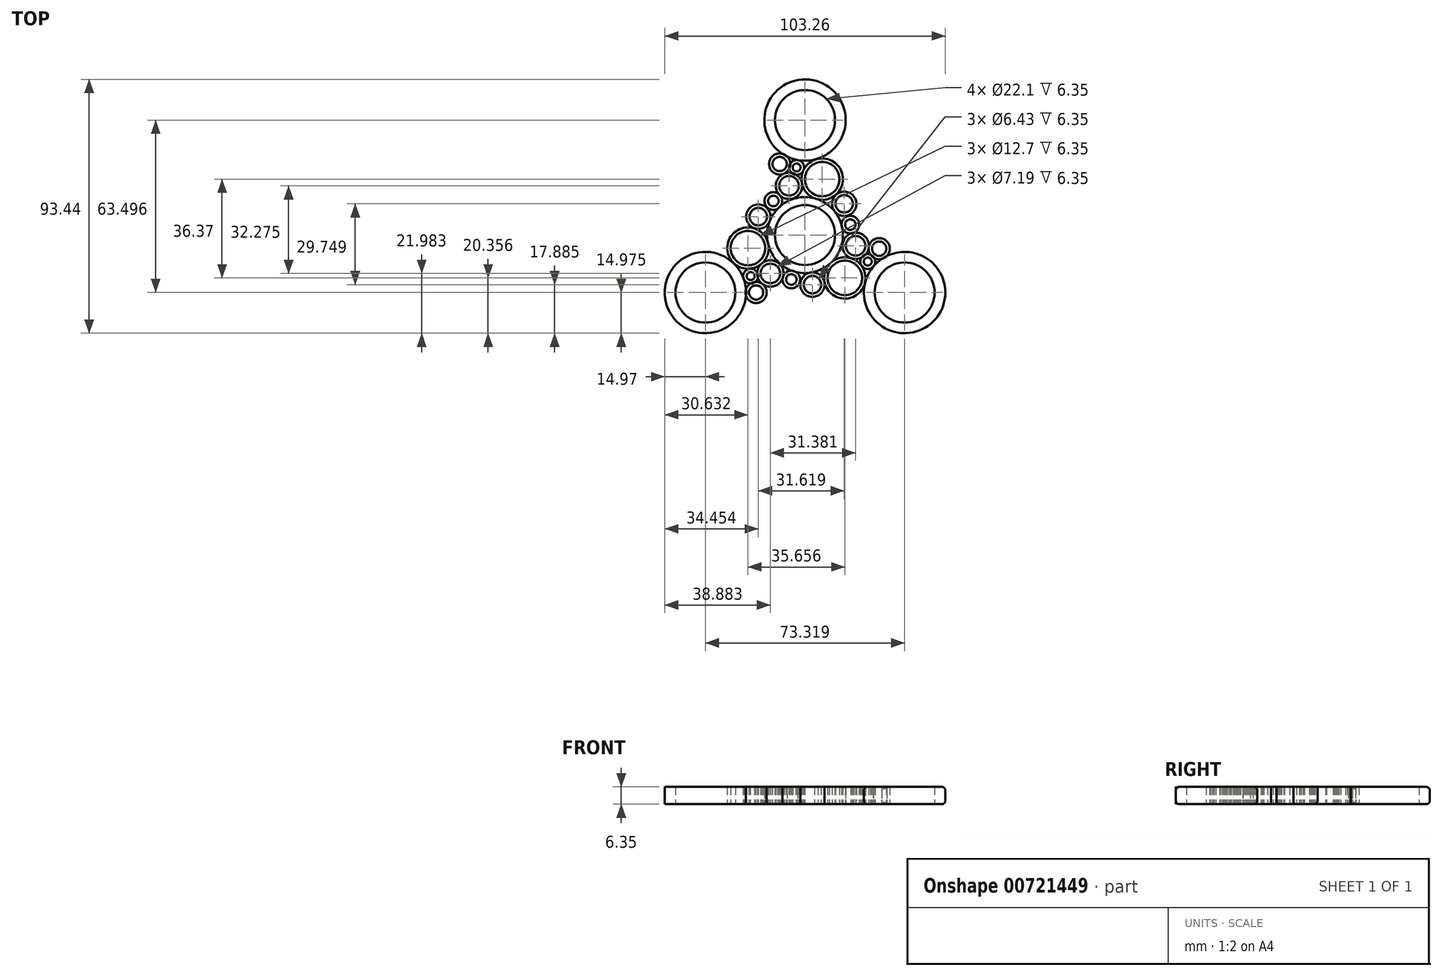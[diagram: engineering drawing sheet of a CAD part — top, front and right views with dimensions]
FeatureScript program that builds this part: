
annotation { "Feature Type Name" : "Feature", "Feature Type Description" : "" }
export const myFeature = defineFeature(function(context is Context, id is Id, definition is map)
    precondition{}
    {
        {
            var Q0;
            Q0=qCreatedBy(makeId("Top.planeOp"),FACE);
            var sketch = newSketch(context, id + "F0", { "sketchPlane" : qUnion([Q0])});
            skCircle(sketch, "E0", {"center": v(0, 0) * mm, "radius": 11.05 * mm});
            skCircle(sketch, "E1", {"center": v(0, 0) * mm, "radius": 13.97 * mm});
            skPoint(sketch, "E2", {"position": v(3.65, 13.49) * mm});
            skCircle(sketch, "E3", {"center": v(6.34, 20.59) * mm, "radius": 7.62 * mm});
            skCircle(sketch, "E4", {"center": v(6.34, 20.59) * mm, "radius": 6.35 * mm});
            skPoint(sketch, "E5", {"position": v(-4.32, 13.29) * mm});
            skPoint(sketch, "E6", {"position": v(-1.17, 19.27) * mm});
            skCircle(sketch, "E7", {"center": v(-5.89, 18.12) * mm, "radius": 4.86 * mm});
            skPoint(sketch, "E8", {"position": v(3.38, 27.75) * mm});
            skCircle(sketch, "E9", {"center": v(0, 42.33) * mm, "radius": 14.97 * mm});
            skCircle(sketch, "E10", {"center": v(0, 42.33) * mm, "radius": 11.05 * mm});
            skPoint(sketch, "E11", {"position": v(-7.51, 22.7) * mm});
            skPoint(sketch, "E12", {"position": v(-6, 24.88) * mm});
            skPoint(sketch, "E13", {"position": v(-7.86, 29.6) * mm});
            skPoint(sketch, "E14", {"position": v(-10.07, 9.68) * mm});
            skCircle(sketch, "E15", {"center": v(-11.66, 12.53) * mm, "radius": 3.26 * mm});
            skCircle(sketch, "E16", {"center": v(-5.89, 18.12) * mm, "radius": 3.6 * mm});
            skPoint(sketch, "E17", {"position": v(-8.94, 14.34) * mm});
            skCircle(sketch, "E18", {"center": v(-11.66, 12.53) * mm, "radius": 1.94 * mm});
            skPoint(sketch, "E19", {"position": v(-3.65, 22.43) * mm});
            skPoint(sketch, "E20", {"position": v(-0.52, 23.91) * mm});
            skCircle(sketch, "E21", {"center": v(-9.31, 26.15) * mm, "radius": 3.9 * mm});
            skCircle(sketch, "E22", {"center": v(-3.09, 24.88) * mm, "radius": 2.75 * mm});
            skPoint(sketch, "E23", {"position": v(-2.54, 27.58) * mm});
            skCircle(sketch, "E24", {"center": v(-3.09, 24.88) * mm, "radius": 1.47 * mm});
            skCircle(sketch, "E25", {"center": v(-9.31, 26.15) * mm, "radius": 2.63 * mm});
            skCircle(sketch, "E26.1.0", {"center": v(-36.66, -21.17) * mm, "radius": 11.05 * mm});
            skCircle(sketch, "E26.2.0", {"center": v(36.66, -21.17) * mm, "radius": 11.05 * mm});
            skCircle(sketch, "E27.1.0", {"center": v(-36.66, -21.17) * mm, "radius": 14.97 * mm});
            skCircle(sketch, "E27.2.0", {"center": v(36.66, -21.17) * mm, "radius": 14.97 * mm});
            skCircle(sketch, "E28.1.0", {"center": v(-21, -4.8) * mm, "radius": 7.62 * mm});
            skCircle(sketch, "E28.2.0", {"center": v(14.66, -15.78) * mm, "radius": 7.62 * mm});
            skCircle(sketch, "E29.1.0", {"center": v(-21, -4.8) * mm, "radius": 6.35 * mm});
            skCircle(sketch, "E29.2.0", {"center": v(14.66, -15.78) * mm, "radius": 6.35 * mm});
            skCircle(sketch, "E30.1.0", {"center": v(-12.75, -14.16) * mm, "radius": 4.86 * mm});
            skCircle(sketch, "E30.2.0", {"center": v(18.63, -3.96) * mm, "radius": 4.86 * mm});
            skCircle(sketch, "E31.1.0", {"center": v(-12.75, -14.16) * mm, "radius": 3.6 * mm});
            skCircle(sketch, "E31.2.0", {"center": v(18.63, -3.96) * mm, "radius": 3.6 * mm});
            skCircle(sketch, "E32.1.0", {"center": v(-5.02, -16.36) * mm, "radius": 3.26 * mm});
            skCircle(sketch, "E32.2.0", {"center": v(16.68, 3.83) * mm, "radius": 3.26 * mm});
            skCircle(sketch, "E33.1.0", {"center": v(-5.02, -16.36) * mm, "radius": 1.94 * mm});
            skCircle(sketch, "E33.2.0", {"center": v(16.68, 3.83) * mm, "radius": 1.94 * mm});
            skCircle(sketch, "E34.1.0", {"center": v(-20, -15.11) * mm, "radius": 2.75 * mm});
            skCircle(sketch, "E34.2.0", {"center": v(23.1, -9.77) * mm, "radius": 2.75 * mm});
            skCircle(sketch, "E35.1.0", {"center": v(-20, -15.11) * mm, "radius": 1.47 * mm});
            skCircle(sketch, "E35.2.0", {"center": v(23.1, -9.77) * mm, "radius": 1.47 * mm});
            skCircle(sketch, "E36.1.0", {"center": v(-18, -21.14) * mm, "radius": 3.9 * mm});
            skCircle(sketch, "E36.2.0", {"center": v(27.3, -5.01) * mm, "radius": 3.9 * mm});
            skCircle(sketch, "E37.1.0", {"center": v(-18, -21.14) * mm, "radius": 2.63 * mm});
            skCircle(sketch, "E37.2.0", {"center": v(27.3, -5.01) * mm, "radius": 2.63 * mm});
            skCircle(sketch, "E38", {"center": v(14.44, 11.5) * mm, "radius": 4.49 * mm});
            skPoint(sketch, "E39", {"position": v(15.34, 6.8) * mm});
            skCircle(sketch, "E40", {"center": v(14.44, 11.5) * mm, "radius": 3.21 * mm});
            skCircle(sketch, "E41.1.0", {"center": v(-17.18, 6.76) * mm, "radius": 4.49 * mm});
            skCircle(sketch, "E41.2.0", {"center": v(2.73, -18.26) * mm, "radius": 4.49 * mm});
            skCircle(sketch, "E42.1.0", {"center": v(-17.18, 6.76) * mm, "radius": 3.21 * mm});
            skCircle(sketch, "E42.2.0", {"center": v(2.73, -18.26) * mm, "radius": 3.21 * mm});
            skSolve(sketch);
        }
        {
            var Q0;
            Q0=makeQuery(id+"F0.imprint","IMPRINT",FACE,{"disambiguationData":[TD([[makeQuery(id+"F0.imprint","IMPRINT",EDGE,{"derivedFrom":sQuery(id+"F0.wireOp",EDGE,"E26.1.0")}),-1.0]])]});
            var Q1;
            Q1=makeQuery(id+"F0.imprint","IMPRINT",FACE,{"disambiguationData":[TD([[makeQuery(id+"F0.imprint","IMPRINT",EDGE,{"derivedFrom":sQuery(id+"F0.wireOp",EDGE,"E37.1.0")}),-1.0]])]});
            var Q2;
            Q2=makeQuery(id+"F0.imprint","IMPRINT",FACE,{"disambiguationData":[TD([[makeQuery(id+"F0.imprint","IMPRINT",EDGE,{"derivedFrom":sQuery(id+"F0.wireOp",EDGE,"E35.1.0")}),-1.0]])]});
            var Q3;
            Q3=makeQuery(id+"F0.imprint","IMPRINT",FACE,{"disambiguationData":[TD([[makeQuery(id+"F0.imprint","IMPRINT",EDGE,{"derivedFrom":sQuery(id+"F0.wireOp",EDGE,"E29.1.0")}),-1.0]])]});
            var Q4;
            Q4=makeQuery(id+"F0.imprint","IMPRINT",FACE,{"disambiguationData":[TD([[makeQuery(id+"F0.imprint","IMPRINT",EDGE,{"derivedFrom":sQuery(id+"F0.wireOp",EDGE,"E31.1.0")}),-1.0]])]});
            var Q5;
            Q5=makeQuery(id+"F0.imprint","IMPRINT",FACE,{"disambiguationData":[TD([[makeQuery(id+"F0.imprint","IMPRINT",EDGE,{"derivedFrom":sQuery(id+"F0.wireOp",EDGE,"E33.1.0")}),-1.0]])]});
            var Q6;
            Q6=makeQuery(id+"F0.imprint","IMPRINT",FACE,{"disambiguationData":[TD([[makeQuery(id+"F0.imprint","IMPRINT",EDGE,{"derivedFrom":sQuery(id+"F0.wireOp",EDGE,"E0")}),-1.0]])]});
            var Q7;
            Q7=makeQuery(id+"F0.imprint","IMPRINT",FACE,{"disambiguationData":[TD([[makeQuery(id+"F0.imprint","IMPRINT",EDGE,{"derivedFrom":sQuery(id+"F0.wireOp",EDGE,"E29.2.0")}),-1.0]])]});
            var Q8;
            Q8=makeQuery(id+"F0.imprint","IMPRINT",FACE,{"disambiguationData":[TD([[makeQuery(id+"F0.imprint","IMPRINT",EDGE,{"derivedFrom":sQuery(id+"F0.wireOp",EDGE,"E26.2.0")}),-1.0]])]});
            var Q9;
            Q9=makeQuery(id+"F0.imprint","IMPRINT",FACE,{"disambiguationData":[TD([[makeQuery(id+"F0.imprint","IMPRINT",EDGE,{"derivedFrom":sQuery(id+"F0.wireOp",EDGE,"E35.2.0")}),-1.0]])]});
            var Q10;
            Q10=makeQuery(id+"F0.imprint","IMPRINT",FACE,{"disambiguationData":[TD([[makeQuery(id+"F0.imprint","IMPRINT",EDGE,{"derivedFrom":sQuery(id+"F0.wireOp",EDGE,"E37.2.0")}),-1.0]])]});
            var Q11;
            Q11=makeQuery(id+"F0.imprint","IMPRINT",FACE,{"disambiguationData":[TD([[makeQuery(id+"F0.imprint","IMPRINT",EDGE,{"derivedFrom":sQuery(id+"F0.wireOp",EDGE,"E31.2.0")}),-1.0]])]});
            var Q12;
            Q12=makeQuery(id+"F0.imprint","IMPRINT",FACE,{"disambiguationData":[TD([[makeQuery(id+"F0.imprint","IMPRINT",EDGE,{"derivedFrom":sQuery(id+"F0.wireOp",EDGE,"E33.2.0")}),-1.0]])]});
            var Q13;
            Q13=makeQuery(id+"F0.imprint","IMPRINT",FACE,{"disambiguationData":[TD([[makeQuery(id+"F0.imprint","IMPRINT",EDGE,{"derivedFrom":sQuery(id+"F0.wireOp",EDGE,"E4")}),-1.0]])]});
            var Q14;
            Q14=makeQuery(id+"F0.imprint","IMPRINT",FACE,{"disambiguationData":[TD([[makeQuery(id+"F0.imprint","IMPRINT",EDGE,{"derivedFrom":sQuery(id+"F0.wireOp",EDGE,"E16")}),-1.0]])]});
            var Q15;
            Q15=makeQuery(id+"F0.imprint","IMPRINT",FACE,{"disambiguationData":[TD([[makeQuery(id+"F0.imprint","IMPRINT",EDGE,{"derivedFrom":sQuery(id+"F0.wireOp",EDGE,"E18")}),-1.0]])]});
            var Q16;
            Q16=makeQuery(id+"F0.imprint","IMPRINT",FACE,{"disambiguationData":[TD([[makeQuery(id+"F0.imprint","IMPRINT",EDGE,{"derivedFrom":sQuery(id+"F0.wireOp",EDGE,"E25")}),-1.0]])]});
            var Q17;
            Q17=makeQuery(id+"F0.imprint","IMPRINT",FACE,{"disambiguationData":[TD([[makeQuery(id+"F0.imprint","IMPRINT",EDGE,{"derivedFrom":sQuery(id+"F0.wireOp",EDGE,"E24")}),-1.0]])]});
            var Q18;
            Q18=makeQuery(id+"F0.imprint","IMPRINT",FACE,{"disambiguationData":[TD([[makeQuery(id+"F0.imprint","IMPRINT",EDGE,{"derivedFrom":sQuery(id+"F0.wireOp",EDGE,"E10")}),-1.0]])]});
            var Q19;
            Q19=makeQuery(id+"F0.imprint","IMPRINT",FACE,{"disambiguationData":[TD([[makeQuery(id+"F0.imprint","IMPRINT",EDGE,{"derivedFrom":sQuery(id+"F0.wireOp",EDGE,"E38")}),1.0]])]});
            var Q20;
            Q20=makeQuery(id+"F0.imprint","IMPRINT",FACE,{"disambiguationData":[TD([[makeQuery(id+"F0.imprint","IMPRINT",EDGE,{"derivedFrom":sQuery(id+"F0.wireOp",EDGE,"E41.1.0")}),1.0]])]});
            var Q21;
            Q21=makeQuery(id+"F0.imprint","IMPRINT",FACE,{"disambiguationData":[TD([[makeQuery(id+"F0.imprint","IMPRINT",EDGE,{"derivedFrom":sQuery(id+"F0.wireOp",EDGE,"E41.2.0")}),1.0]])]});
            extrude(context, id + "F1", {"entities" : qUnion([Q0, Q1, Q2, Q3, Q4, Q5, Q6, Q7, Q8, Q9, Q10, Q11, Q12, Q13, Q14, Q15, Q16, Q17, Q18, Q19, Q20, Q21]), "depth" : 6.35 * mm, "offsetDistance" : 25.4 * mm});
        }
        {
            var Q0;
            {var subQ0=sQuery(id+"F0.wireOp",EDGE,"E27.1.0");Q0=makeQuery(id+"F1.opExtrude","CAP_EDGE",EDGE,{"disambiguationData":[OSD([subQ0]),TDD([makeQuery(id+"F0.imprint","IMPRINT",EDGE,{"disambiguationData":[TD([[makeQuery(id+"F0.imprint","INTERSECT",VERTEX,{"disambiguationData":[OD(0.0)],"derivedFrom":[subQ0,sQuery(id+"F0.wireOp",EDGE,"E36.1.0")]}),1.0]])],"derivedFrom":subQ0})])],"isStart":false});}
            var Q1;
            {var subQ0=sQuery(id+"F0.wireOp",EDGE,"E27.1.0");Q1=makeQuery(id+"F1.opExtrude","CAP_EDGE",EDGE,{"disambiguationData":[OSD([subQ0]),TDD([makeQuery(id+"F0.imprint","IMPRINT",EDGE,{"disambiguationData":[TD([[makeQuery(id+"F0.imprint","INTERSECT",VERTEX,{"disambiguationData":[OD(0.0)],"derivedFrom":[subQ0,sQuery(id+"F0.wireOp",EDGE,"E36.1.0")]}),1.0]])],"derivedFrom":subQ0})])],"isStart":true});}
            var Q2;
            {var subQ0=sQuery(id+"F0.wireOp",EDGE,"E27.2.0");Q2=makeQuery(id+"F1.opExtrude","CAP_EDGE",EDGE,{"disambiguationData":[OSD([subQ0]),TDD([makeQuery(id+"F0.imprint","IMPRINT",EDGE,{"disambiguationData":[TD([[makeQuery(id+"F0.imprint","INTERSECT",VERTEX,{"disambiguationData":[OD(0.0)],"derivedFrom":[subQ0,sQuery(id+"F0.wireOp",EDGE,"E36.2.0")]}),1.0]])],"derivedFrom":subQ0})])],"isStart":false});}
            var Q3;
            {var subQ0=sQuery(id+"F0.wireOp",EDGE,"E27.2.0");Q3=makeQuery(id+"F1.opExtrude","CAP_EDGE",EDGE,{"disambiguationData":[OSD([subQ0]),TDD([makeQuery(id+"F0.imprint","IMPRINT",EDGE,{"disambiguationData":[TD([[makeQuery(id+"F0.imprint","INTERSECT",VERTEX,{"disambiguationData":[OD(0.0)],"derivedFrom":[subQ0,sQuery(id+"F0.wireOp",EDGE,"E36.2.0")]}),1.0]])],"derivedFrom":subQ0})])],"isStart":true});}
            var Q4;
            {var subQ0=sQuery(id+"F0.wireOp",EDGE,"E9");Q4=makeQuery(id+"F1.opExtrude","CAP_EDGE",EDGE,{"disambiguationData":[OSD([subQ0]),TDD([makeQuery(id+"F0.imprint","IMPRINT",EDGE,{"disambiguationData":[TD([[makeQuery(id+"F0.imprint","INTERSECT",VERTEX,{"disambiguationData":[OD(0.0)],"derivedFrom":[sQuery(id+"F0.wireOp",EDGE,"E21"),subQ0]}),1.0]])],"derivedFrom":subQ0})])],"isStart":false});}
            var Q5;
            {var subQ0=sQuery(id+"F0.wireOp",EDGE,"E9");Q5=makeQuery(id+"F1.opExtrude","CAP_EDGE",EDGE,{"disambiguationData":[OSD([subQ0]),TDD([makeQuery(id+"F0.imprint","IMPRINT",EDGE,{"disambiguationData":[TD([[makeQuery(id+"F0.imprint","INTERSECT",VERTEX,{"disambiguationData":[OD(0.0)],"derivedFrom":[sQuery(id+"F0.wireOp",EDGE,"E21"),subQ0]}),1.0]])],"derivedFrom":subQ0})])],"isStart":true});}
            fillet(context, id + "F2", {"entities" : qUnion([Q0, Q1, Q2, Q3, Q4, Q5]), "radius" : 1.27 * mm, "tangentPropagation" : true, "allowEdgeOverflow" : false});
        }
        {
            var Q0;
            Q0=makeQuery(id+"F1.opExtrude","CAP_EDGE",EDGE,{"disambiguationData":[OSD([sQuery(id+"F0.wireOp",EDGE,"E38")])],"isStart":true});
            fillet(context, id + "F3", {"entities" : qUnion([Q0]), "radius" : 1.27 * mm, "tangentPropagation" : true, "allowEdgeOverflow" : false});
        }
    });
